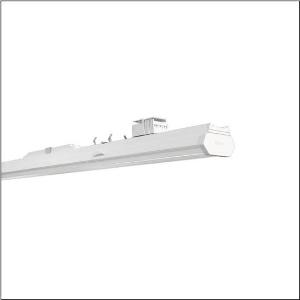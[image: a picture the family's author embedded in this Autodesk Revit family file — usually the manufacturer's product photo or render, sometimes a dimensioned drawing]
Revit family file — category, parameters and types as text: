
# Revit family: licross_r__11_protected_ho_51td1bdn4e5m3c_9259
name_source: partatom
category: Lighting Fixtures
units: mm (PartAtom-declared; Revit-internal decimal feet)

## family parameters
Cut with Voids When Loaded = No
Host = Face
Light Source = No
Part Type = Normal
Room Calculation Point = No
Round Connector Dimension = Use Diameter
Shared = No

## types (1)
- --- (1 x LED, 920 lm, 7.4 W, 4000K)
    Apparent Load = 7 VA
    CIE Flux Codes = 54 82 95 97 100
    Color Rendering = 80
    Color Temperature = 4000K
    Default Elevation = 1800 mm
    Description = Licross® 11 Protected HO, luminaire insert, of sheet steel, galvanised, coil coated, white, length: 1.500mm, width: 90mm, height: 101mm, LED rated luminous flux: 14.500lm, light colour: 840, control gear: DALI 2 (for two DALI lines), with plug, 6-pole, with phase selection, for trunking rail, 14-core, mains connection: 220..240V, AC, 50/60Hz, rated input power: 91W, for trunking rail, 14-core, halogen-free wiring, for emergency light function, converter,control gear: single battery element, battery: LiFePO4, 9Ah, primary optical cover: cover, of PMMA, light emission: direct distribution, primary light characteristic: symmetric, protection rating (complete): IP54, insulation class (complete): insulation class I (protective earthing), certification: CE, UKCA, protection symbol: D if used in an environment with non-conductive dust loads with corresponding accessories, impact resistance: IK06, permissible ambient temperature for indoor applications: +5..+30°C, standard: EN 60598-2-22, LABS conformity tested according to VDMA 24364:2018-05, reducing of maximum allowable ambient temperature of 5°C with ceiling mounting, corresponds to IFS (International Featured Standards) requirements for safety and quality in the food industry, packaging unit: 1 piece
    Height = 92 mm
    Lamp = 1 x LED
    Lamp Light Flux = 920 lm
    Lamp Power = 7.4 W
    Lamp count = 1
    Length = 1500 mm
    Luminous efficacy = 124 lm/W
    Manufacturer = Siteco
    ModVariant = No
    Model = 51TD1BDN4E5M3C
    Mounting Place = Ceiling
    Mounting Type = Pendant
    Number of Poles = 1
    OnlyDefault = Yes
    Power Factor = 1
    Product Name = Licross® 11 Protected HO
    Product group = luminaire insert
    ProductGroupID = 901
    Protection Class = Protection class I
    Protection Degree = IP 54
    RLX_Detail_Level = 1
    RLX_Emergency_Light_Flux = 0 lm
    RLX_Emergency_Type = 0
    RLX_Emergency_Type_DB = No
    RlxData = <blob elided: 24729 chars, md5=c3b79fa1>
    Socket = socket
    Standby Power = 0 W
    System Light Flux = 920 lm
    System Power = 7 W
    Type Comments = : emergency light operation: 3 h
    Type Image = l_1256145.jpg
    URL = http://relux.com
    VarID = @adj_060059
    Voltage = 0 V
    Weight = 0.00 kg
    Width = 88 mm

## geometry (parser evidence)
native form markers: Blend x4, Sweep x11
no freeform markers — native parametric forms only
